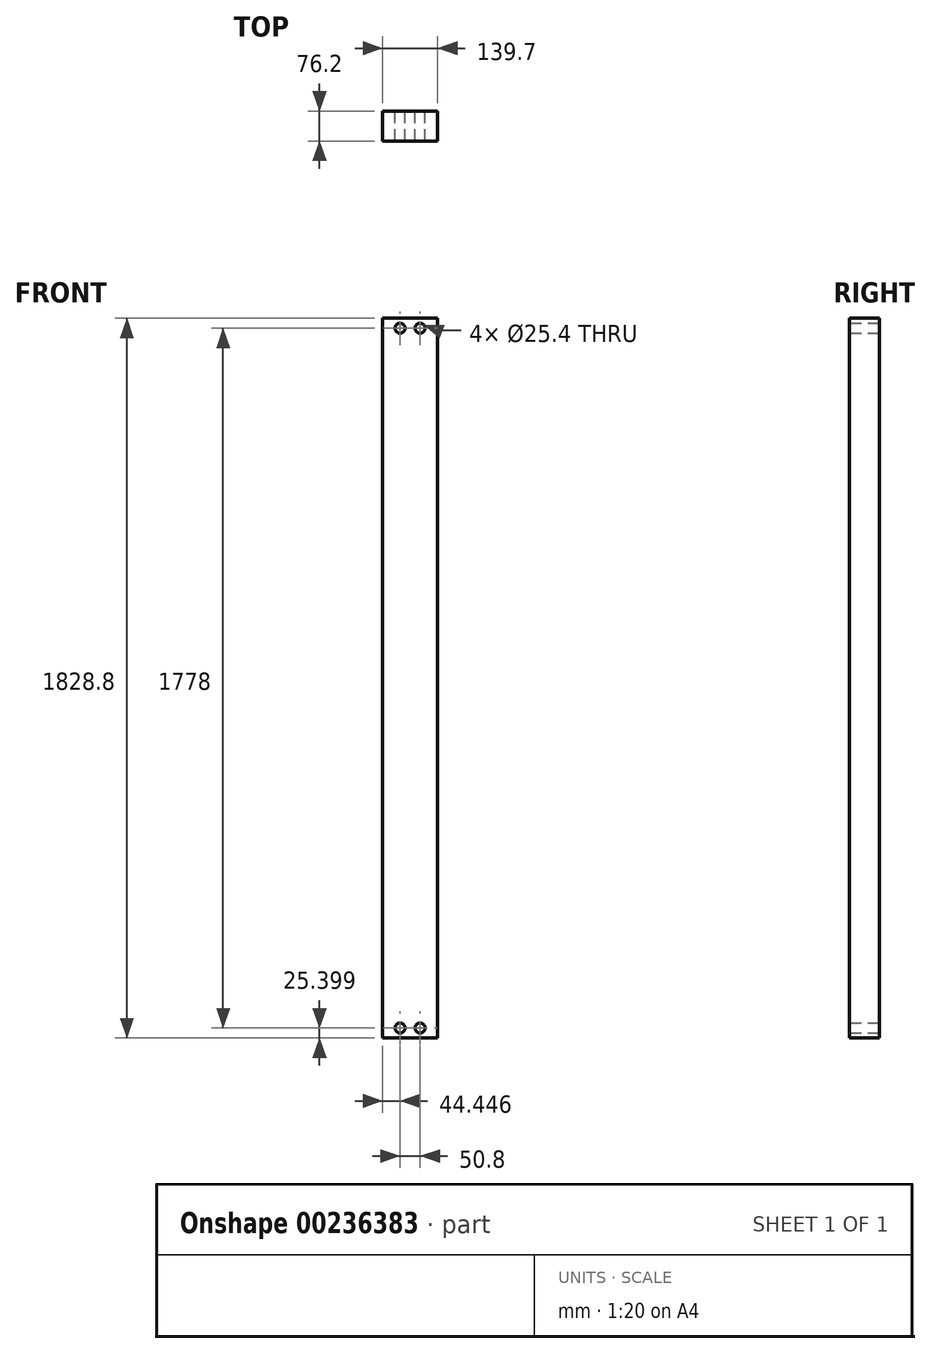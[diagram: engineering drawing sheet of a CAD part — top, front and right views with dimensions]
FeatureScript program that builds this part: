
annotation { "Feature Type Name" : "Feature", "Feature Type Description" : "" }
export const myFeature = defineFeature(function(context is Context, id is Id, definition is map)
    precondition{}
    {
        {
            var Q0;
            Q0=qCreatedBy(makeId("Front.planeOp"),FACE);
            var sketch = newSketch(context, id + "F0", { "sketchPlane" : qUnion([Q0])});
            skLineSegment(sketch, "E0.bottom", {"start": v(-476.3, 933.04) * mm, "end": v(-336.6, 933.04) * mm});
            skLineSegment(sketch, "E0.top", {"start": v(-476.3, -895.76) * mm, "end": v(-336.6, -895.76) * mm});
            skLineSegment(sketch, "E0.left", {"start": v(-476.3, 933.04) * mm, "end": v(-476.3, -895.76) * mm});
            skLineSegment(sketch, "E0.right", {"start": v(-336.6, 933.04) * mm, "end": v(-336.6, -895.76) * mm});
            skCircle(sketch, "E1", {"center": v(-431.85, 907.64) * mm, "radius": 12.7 * mm});
            skCircle(sketch, "E2", {"center": v(-381.05, 907.64) * mm, "radius": 12.7 * mm});
            skCircle(sketch, "E3", {"center": v(-431.85, -870.36) * mm, "radius": 12.7 * mm});
            skCircle(sketch, "E4", {"center": v(-381.05, -870.36) * mm, "radius": 12.7 * mm});
            skSolve(sketch);
        }
        {
            var Q0;
            Q0 = qSketchRegion(id + "F0", true);
            extrude(context, id + "F1", {"entities" : qUnion([Q0]), "depth" : 76.2 * mm});
        }
    });
